# Revit family: Acoustic-Control_Wenger_Transform-Banner-Fabric-Fabric
name_source: partatom
category: Generic Models
revit_build: Autodesk Revit 2016 (Build: 20161004_0715(x64)
units: mm (PartAtom-declared; Revit-internal decimal feet)

## family parameters
Always vertical = No
Can host rebar = No
Cut with Voids When Loaded = No
Part Type = Normal
Room Calculation Point = No
Round Connector Dimension = Use Diameter
Shared = No
Work Plane-Based = Yes

## types (4) — shared parameters
Assembly Code = E1020300
Banner Length = 15' - 0"
Construction Details = http://www.arcat.com
Default Elevation = 0' - 0"
Description = Wenger Wall Mounted Motorized Acoustic Banner - Transform Fabric Fabric as Specified
Green Building-LEED = http://www.arcat.com
Keynote = 11 60 01
Manufacturer = Wenger Corporation
Manufacturer Website = https://www.wengercorp.com
Model = Transform Fabric Fabric
Product Data = http://www.arcat.com
Revision = R1_2017-12
Sales Information = https://www.wengercorp.com
SpecWizard = http://www.arcat.com
Specification = http://www.arcat.com
Standards Conformance = Fabrics IFR Rated
URL = https://www.wengercorp.com
Unit Depth = 1' - 0"
Unit Height = 1' - 8"
Unit Width = 2' - 8"
zero-valued in all types: Expected Lifespan (Years), Maintenance Schedule (Months), Warranty Duration (Years)

## per-type parameters (varying)
| type | Banner Length Range | Banner Width Range |
| Wool Extra Wide Fabric | Up to 15 ft | 68.5" - 124.5" |
| Velour Extra Wide Fabric | Up to 15 ft | 71.5" - 124.5" |
| Wool Standard Width Fabric | Up to 30 ft | 38.5" - 64.5" |
| Velour Standard Width Fabric | Up to 30 ft | 38.5" - 70.5" |

## geometry (parser evidence)
native form markers: Sweep x2
no freeform markers — native parametric forms only
